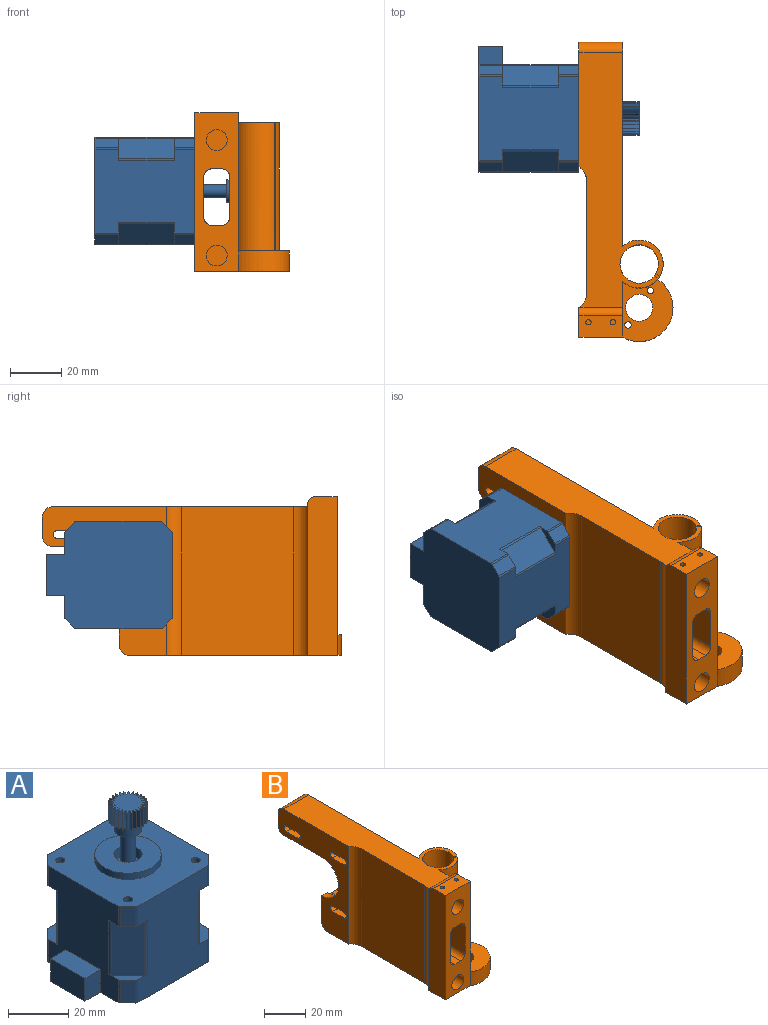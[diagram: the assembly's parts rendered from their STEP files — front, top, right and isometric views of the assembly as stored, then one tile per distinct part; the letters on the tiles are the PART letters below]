
ASSEMBLY  parts=2 mates=1
PART A: 123 faces, bbox 49.2x42x62.5 mm
  f0: cylinder r=2.5mm len=14mm, axis (0,0,-1), area 219.9mm2, adj f66,f68
  f1: plane 42x42mm, normal (0,0,1), area 1319.4mm2, adj f5,f7,f9,f11,f22,f23,f24,f25
  f2: plane 8.9x8.9mm, normal (0,0,1), area 27mm2, adj f5,f11,f12,f15,f35,f42,f49,f50
  f3: plane 8.9x8.9mm, normal (0,0,1), area 27mm2, adj f7,f8,f9,f17,f38,f39,f45,f46
  f4: plane 8.9x8.9mm, normal (0,0,1), area 27mm2, adj f9,f10,f11,f18,f40,f41,f47,f48
  f5: plane 39x32.69mm, normal (0,1,0), area 1089.8mm2, adj f1,f2,f13,f14,f19,f20,f28,f33
  f6: plane 9.2x3.66mm, normal (-0.71,0.71,0), area 47.6mm2, adj f13,f14,f43,f44
  f7: plane 39x32.69mm, normal (-1,0,0), area 941.7mm2, adj f1,f3,f13,f14,f19,f26,f31,f34
  f8: plane 9.2x3.66mm, normal (-0.71,-0.71,0), area 47.6mm2, adj f3,f14,f45,f46
  f9: plane 39x32.69mm, normal (0,-1,0), area 1089.8mm2, adj f1,f3,f4,f14,f21,f26,f29,f32
  f10: plane 9.2x3.66mm, normal (0.71,-0.71,0), area 47.6mm2, adj f4,f14,f47,f48
  f11: plane 39x32.69mm, normal (1,0,0), area 1089.8mm2, adj f1,f2,f4,f14,f20,f21,f27,f30
  f12: plane 9.2x3.66mm, normal (0.71,0.71,0), area 47.6mm2, adj f2,f14,f49,f50
  f13: plane 8.9x8.9mm, normal (0,0,1), area 27mm2, adj f5,f6,f7,f16,f36,f37,f43,f44
  f14: plane 49.2x42mm, normal (0,0,-1), area 1843.7mm2, adj f5,f6,f7,f8,f9,f10,f11,f12
  f15: plane 21.8x7.9mm, normal (0.71,0.71,0), area 243.5mm2, adj f2,f20,f35,f42
  f16: plane 21.8x7.9mm, normal (-0.71,0.71,0), area 243.5mm2, adj f13,f19,f36,f37
  f17: plane 21.8x7.9mm, normal (-0.71,-0.71,0), area 243.5mm2, adj f3,f26,f38,f39
  f18: plane 21.8x7.9mm, normal (0.71,-0.71,0), area 243.5mm2, adj f4,f21,f40,f41
  f19: plane 8.9x8.9mm, normal (0,0,-1), area 27mm2, adj f5,f7,f16,f23,f33,f34,f36,f37
  f20: plane 8.9x8.9mm, normal (0,0,-1), area 27mm2, adj f5,f11,f15,f22,f27,f28,f35,f42
  f21: plane 8.9x8.9mm, normal (0,0,-1), area 27mm2, adj f9,f11,f18,f25,f29,f30,f40,f41
  f22: plane 8x3.66mm, normal (0.71,0.71,0), area 41.4mm2, adj f1,f20,f27,f28
  f23: plane 8x3.66mm, normal (-0.71,0.71,0), area 41.4mm2, adj f1,f19,f33,f34
  f24: plane 8x3.66mm, normal (-0.71,-0.71,0), area 41.4mm2, adj f1,f26,f31,f32
  f25: plane 8x3.66mm, normal (0.71,-0.71,0), area 41.4mm2, adj f1,f21,f29,f30
  f26: plane 8.9x8.9mm, normal (0,0,-1), area 27mm2, adj f7,f9,f17,f24,f31,f32,f38,f39
  f27: cylinder r=1mm len=8mm, axis (0,0,1), area 6.3mm2, adj f1,f11,f20,f22
  f28: cylinder r=1mm len=8mm, axis (0,0,-1), area 6.3mm2, adj f1,f5,f20,f22
  f29: cylinder r=1mm len=8mm, axis (0,0,-1), area 6.3mm2, adj f1,f9,f21,f25
  f30: cylinder r=1mm len=8mm, axis (0,0,-1), area 6.3mm2, adj f1,f11,f21,f25
  f31: cylinder r=1mm len=8mm, axis (0,0,-1), area 6.3mm2, adj f1,f7,f24,f26
  f32: cylinder r=1mm len=8mm, axis (0,0,1), area 6.3mm2, adj f1,f9,f24,f26
  f33: cylinder r=1mm len=8mm, axis (0,0,1), area 6.3mm2, adj f1,f5,f19,f23
  f34: cylinder r=1mm len=8mm, axis (0,0,1), area 6.3mm2, adj f1,f7,f19,f23
  f35: cylinder r=1mm len=21.8mm, axis (0,0,-1), area 17.1mm2, adj f2,f5,f15,f20
  f36: cylinder r=1mm len=21.8mm, axis (0,0,1), area 17.1mm2, adj f5,f13,f16,f19
  f37: cylinder r=1mm len=21.8mm, axis (0,0,1), area 17.1mm2, adj f7,f13,f16,f19
  f38: cylinder r=1mm len=21.8mm, axis (0,0,-1), area 17.1mm2, adj f3,f7,f17,f26
  f39: cylinder r=1mm len=21.8mm, axis (0,0,1), area 17.1mm2, adj f3,f9,f17,f26
  f40: cylinder r=1mm len=21.8mm, axis (0,0,-1), area 17.1mm2, adj f4,f9,f18,f21
  f41: cylinder r=1mm len=21.8mm, axis (0,0,-1), area 17.1mm2, adj f4,f11,f18,f21
  f42: cylinder r=1mm len=21.8mm, axis (0,0,1), area 17.1mm2, adj f2,f11,f15,f20
  f43: cylinder r=1mm len=9.2mm, axis (0,0,1), area 7.2mm2, adj f5,f6,f13,f14
  f44: cylinder r=1mm len=9.2mm, axis (0,0,1), area 7.2mm2, adj f6,f7,f13,f14
  f45: cylinder r=1mm len=9.2mm, axis (0,0,-1), area 7.2mm2, adj f3,f7,f8,f14
  f46: cylinder r=1mm len=9.2mm, axis (0,0,1), area 7.2mm2, adj f3,f8,f9,f14
  f47: cylinder r=1mm len=9.2mm, axis (0,0,-1), area 7.2mm2, adj f4,f9,f10,f14
  f48: cylinder r=1mm len=9.2mm, axis (0,0,-1), area 7.2mm2, adj f4,f10,f11,f14
  f49: cylinder r=1mm len=9.2mm, axis (0,0,1), area 7.2mm2, adj f2,f11,f12,f14
  f50: cylinder r=1mm len=9.2mm, axis (0,0,-1), area 7.2mm2, adj f2,f5,f12,f14
  f51: plane 16.1x7.2mm, normal (0,0,1), area 115.9mm2, adj f7,f52,f53,f54
  f52: plane 9.2x7.2mm, normal (0,1,0), area 66.2mm2, adj f7,f14,f51,f54
  f53: plane 9.2x7.2mm, normal (0,-1,0), area 66.2mm2, adj f7,f14,f51,f54
  f54: plane 16.1x9.2mm, normal (-1,0,0), area 148.1mm2, adj f14,f51,f52,f53
  f55: cylinder r=1.5mm len=5.6mm, axis (0,0,1), area 52.8mm2, adj f1,f56
  f56: plane 3x3mm, normal (0,0,1), area 7.1mm2, adj f55
  f57: cylinder r=1.5mm len=5.6mm, axis (0,0,1), area 52.8mm2, adj f1,f58
  f58: plane 3x3mm, normal (0,0,1), area 7.1mm2, adj f57
  f59: cylinder r=1.5mm len=5.6mm, axis (0,0,1), area 52.8mm2, adj f1,f60
  f60: plane 3x3mm, normal (0,0,1), area 7.1mm2, adj f59
  f61: cylinder r=1.5mm len=5.6mm, axis (0,0,1), area 52.8mm2, adj f1,f62
  f62: plane 3x3mm, normal (0,0,1), area 7.1mm2, adj f61
  f63: cylinder r=11mm len=22mm, axis (0,0,-1), area 172.8mm2, adj f1,f64
  f64: plane 22x22mm, normal (0,0,1), area 312.2mm2, adj f63,f65
  f65: cylinder r=4.65mm len=9.3mm, axis (0,0,1), area 116.9mm2, adj f64,f66
  f66: plane 9.3x9.3mm, normal (0,0,1), area 48.3mm2, adj f0,f65
  f67: cylinder r=4.5mm len=9mm, axis (0,0,1), area 113.1mm2, adj f68,f72
  f68: plane 9x9mm, normal (0,0,-1), area 44mm2, adj f0,f67
  f69: plane 12.99x12.95mm, normal (0,0,1), area 96.3mm2, adj f70,f71,f73,f74,f75,f76,f77,f78
  f70: plane 7x1.39mm, normal (-0.73,0.68,0), area 13.3mm2, adj f69,f71,f72,f122
  f71: plane 7x1.85mm, normal (0.21,-0.98,0), area 13.3mm2, adj f69,f70,f72,f73
  f72: plane 12.99x12.95mm, normal (0,0,-1), area 32.7mm2, adj f67,f70,f71,f73,f74,f75,f76,f77
  f73: plane 7x1.66mm, normal (-0.87,0.49,0), area 13.3mm2, adj f69,f71,f72,f74
  f74: plane 7x1.71mm, normal (0.44,-0.9,0), area 13.3mm2, adj f69,f72,f73,f75
  f75: plane 7x1.83mm, normal (-0.96,0.26,0), area 13.3mm2, adj f69,f72,f74,f76
  f76: plane 7x1.46mm, normal (0.64,-0.77,0), area 13.3mm2, adj f69,f72,f75,f77
  f77: plane 7x1.89mm, normal (-1,0.03,0), area 13.3mm2, adj f69,f72,f76,f78
  f78: plane 7x1.52mm, normal (0.8,-0.59,0), area 13.3mm2, adj f69,f72,f77,f79
  f79: plane 7x1.85mm, normal (-0.98,-0.21,0), area 13.3mm2, adj f69,f72,f78,f80
  f80: plane 7x1.75mm, normal (0.92,-0.38,0), area 13.3mm2, adj f69,f72,f79,f81
  f81: plane 7x1.7mm, normal (-0.9,-0.44,0), area 13.3mm2, adj f69,f72,f80,f82
  f82: plane 7x1.87mm, normal (0.99,-0.15,0), area 13.3mm2, adj f69,f72,f81,f83
  f83: plane 7x1.45mm, normal (-0.76,-0.64,0), area 13.3mm2, adj f69,f72,f82,f84
  f84: plane 7x1.89mm, normal (1,0.09,0), area 13.3mm2, adj f69,f72,f83,f85
  f85: plane 7x1.53mm, normal (-0.59,-0.81,0), area 13.3mm2, adj f69,f72,f84,f86
  f86: plane 7x1.79mm, normal (0.95,0.32,0), area 13.3mm2, adj f69,f72,f85,f87
  f87: plane 7x1.75mm, normal (-0.38,-0.93,0), area 13.3mm2, adj f69,f72,f86,f88
  f88: plane 7x1.59mm, normal (0.84,0.54,0), area 13.3mm2, adj f69,f72,f87,f89
  f89: plane 7x1.87mm, normal (-0.15,-0.99,0), area 13.3mm2, adj f69,f72,f88,f90
  f90: plane 7x1.38mm, normal (0.69,0.73,0), area 13.3mm2, adj f69,f72,f89,f91
  f91: plane 7x1.89mm, normal (0.1,-1,0), area 13.3mm2, adj f69,f72,f90,f92
  f92: plane 7x1.65mm, normal (0.49,0.87,0), area 13.3mm2, adj f69,f72,f91,f93
  f93: plane 7x1.79mm, normal (0.33,-0.94,0), area 13.3mm2, adj f69,f72,f92,f94
  f94: plane 7x1.82mm, normal (0.27,0.96,0), area 13.3mm2, adj f69,f72,f93,f95
  f95: plane 7x1.59mm, normal (0.55,-0.84,0), area 13.3mm2, adj f69,f72,f94,f96
  f96: plane 7x1.89mm, normal (0.03,1,0), area 13.3mm2, adj f69,f72,f95,f97
  f97: plane 7x1.39mm, normal (0.73,-0.68,0), area 13.3mm2, adj f69,f72,f96,f98
  f98: plane 7x1.85mm, normal (-0.21,0.98,0), area 13.3mm2, adj f69,f72,f97,f99
  f99: plane 7x1.66mm, normal (0.87,-0.49,0), area 13.3mm2, adj f69,f72,f98,f100
  f100: plane 7x1.71mm, normal (-0.44,0.9,0), area 13.3mm2, adj f69,f72,f99,f101
  f101: plane 7x1.83mm, normal (0.96,-0.26,0), area 13.3mm2, adj f69,f72,f100,f102
  f102: plane 7x1.46mm, normal (-0.64,0.77,0), area 13.3mm2, adj f69,f72,f101,f103
  f103: plane 7x1.89mm, normal (1,-0.03,0), area 13.3mm2, adj f69,f72,f102,f104
  f104: plane 7x1.52mm, normal (-0.8,0.59,0), area 13.3mm2, adj f69,f72,f103,f105
  f105: plane 7x1.85mm, normal (0.98,0.21,0), area 13.3mm2, adj f69,f72,f104,f106
  f106: plane 7x1.75mm, normal (-0.92,0.38,0), area 13.3mm2, adj f69,f72,f105,f107
  f107: plane 7x1.7mm, normal (0.9,0.44,0), area 13.3mm2, adj f69,f72,f106,f108
  f108: plane 7x1.87mm, normal (-0.99,0.15,0), area 13.3mm2, adj f69,f72,f107,f109
  f109: plane 7x1.45mm, normal (0.76,0.64,0), area 13.3mm2, adj f69,f72,f108,f110
  f110: plane 7x1.89mm, normal (-1,-0.09,0), area 13.3mm2, adj f69,f72,f109,f111
  f111: plane 7x1.53mm, normal (0.59,0.81,0), area 13.3mm2, adj f69,f72,f110,f112
  f112: plane 7x1.79mm, normal (-0.95,-0.32,0), area 13.3mm2, adj f69,f72,f111,f113
  f113: plane 7x1.75mm, normal (0.38,0.93,0), area 13.3mm2, adj f69,f72,f112,f114
  f114: plane 7x1.59mm, normal (-0.84,-0.54,0), area 13.3mm2, adj f69,f72,f113,f115
  f115: plane 7x1.87mm, normal (0.15,0.99,0), area 13.3mm2, adj f69,f72,f114,f116
  f116: plane 7x1.38mm, normal (-0.69,-0.73,0), area 13.3mm2, adj f69,f72,f115,f117
  f117: plane 7x1.89mm, normal (-0.1,1,0), area 13.3mm2, adj f69,f72,f116,f118
  f118: plane 7x1.65mm, normal (-0.49,-0.87,0), area 13.3mm2, adj f69,f72,f117,f119
  f119: plane 7x1.79mm, normal (-0.33,0.94,0), area 13.3mm2, adj f69,f72,f118,f120
  f120: plane 7x1.82mm, normal (-0.27,-0.96,0), area 13.3mm2, adj f69,f72,f119,f121
  f121: plane 7x1.59mm, normal (-0.55,0.84,0), area 13.3mm2, adj f69,f72,f120,f122
  f122: plane 7x1.89mm, normal (-0.03,-1,0), area 13.3mm2, adj f69,f70,f72,f121
PART B: 73 faces, bbox 36.7x116.7x62 mm
  f0: plane 99.5x32.86mm, normal (0,0,1), area 1607.2mm2, adj f1,f16,f17,f18,f19,f20,f21,f22
  f1: plane 79.76x58mm, normal (1,0,0), area 2945.1mm2, adj f0,f15,f20,f24,f33,f34,f35,f44
  f2: cylinder r=1.6mm len=15mm, axis (-1,0,0), area 75.4mm2, adj f3,f5,f21,f61
  f3: plane 15x7.89mm, normal (0,0,-1), area 118.4mm2, adj f2,f4,f21,f61
  f4: cylinder r=1.6mm len=15mm, axis (-1,0,0), area 75.4mm2, adj f3,f5,f21,f61
  f5: plane 15x7.89mm, normal (0,0,1), area 118.4mm2, adj f2,f4,f21,f61
  f6: cylinder r=1.6mm len=15mm, axis (-1,0,0), area 75.4mm2, adj f7,f9,f21,f56
  f7: plane 15x8mm, normal (0,0,-1), area 120mm2, adj f6,f8,f21,f56
  f8: cylinder r=1.6mm len=15mm, axis (-1,0,0), area 75.4mm2, adj f7,f9,f21,f56
  f9: plane 15x8mm, normal (0,0,1), area 120mm2, adj f6,f8,f21,f56
  f10: cylinder r=1.6mm len=15mm, axis (-1,0,0), area 75.4mm2, adj f11,f13,f21,f51
  f11: plane 15x8mm, normal (0,0,-1), area 120mm2, adj f10,f12,f21,f51
  f12: cylinder r=1.6mm len=15mm, axis (-1,0,0), area 75.4mm2, adj f11,f13,f21,f51
  f13: plane 15x8mm, normal (0,0,1), area 120mm2, adj f10,f12,f21,f51
  f14: plane 62x17mm, normal (0,-1,0), area 737.3mm2, adj f16,f23,f24,f25,f36,f37,f38,f39
  f15: plane 17x15.5mm, normal (0,1,0), area 252mm2, adj f1,f21,f35,f36,f46,f69,f72
  f16: plane 54x21.76mm, normal (1,0,0), area 1132mm2, adj f0,f14,f20,f29,f62,f65,f68
  f17: plane 57x1.46mm, normal (0.63,0.78,0), area 106.6mm2, adj f0,f18,f20,f30
  f18: cylinder r=7.49mm len=58mm, axis (0,0,-1), area 2677.8mm2, adj f0,f17,f19,f24,f30
  f19: plane 57x1.47mm, normal (-0.63,-0.78,0), area 107.5mm2, adj f0,f18,f20,f30
  f20: cylinder r=9.36mm len=58mm, axis (0,0,-1), area 2363.1mm2, adj f0,f1,f16,f17,f19,f24,f25,f29
  f21: plane 58x48.5mm, normal (-1,0,0), area 1219.4mm2, adj f0,f2,f3,f4,f5,f6,f7,f8
  f22: plane 58x43.76mm, normal (-1,0,0), area 2538.3mm2, adj f0,f24,f31,f32
  f23: plane 62x11.5mm, normal (-1,0,0), area 711.1mm2, adj f14,f24,f32,f62,f65,f68
  f24: plane 82.71x36.71mm, normal (0,0,-1), area 1581.7mm2, adj f1,f14,f18,f20,f21,f22,f23,f25
  f25: cylinder r=13.21mm len=24.26mm, axis (0,0,-1), area 325.1mm2, adj f14,f20,f24,f29
  f26: cylinder r=1.22mm len=8mm, axis (0,0,-1), area 61.6mm2, adj f24,f29
  f27: cylinder r=1.25mm len=8mm, axis (0,0,-1), area 62.8mm2, adj f24,f29
  f28: cylinder r=5.25mm len=10.5mm, axis (0,0,-1), area 263.9mm2, adj f24,f29
  f29: plane 24.26x19.71mm, normal (0,0,1), area 287.3mm2, adj f16,f20,f25,f26,f27,f28
  f30: plane 1.99x1.94mm, normal (0,0,1), area 1.7mm2, adj f17,f18,f19,f20
  f31: cylinder r=6.76mm len=58mm, axis (0,0,1), area 384.6mm2, adj f0,f21,f22,f24
  f32: cylinder r=6.76mm len=58mm, axis (0,0,1), area 384.6mm2, adj f0,f22,f23,f24
  f33: plane 26x17mm, normal (0,0,-1), area 442mm2, adj f1,f21,f35,f45
  f34: plane 17x7.5mm, normal (0,1,0), area 127.5mm2, adj f1,f21,f44,f45
  f35: cylinder r=11.5mm len=23mm, axis (-1,0,0), area 338.2mm2, adj f1,f15,f21,f33,f37,f38,f39,f69
  f36: plane 85x4mm, normal (0,0,1), area 340mm2, adj f14,f15,f69,f72
  f37: plane 79.32x16mm, normal (-1,0,0), area 1196.2mm2, adj f14,f35,f69,f70
  f38: plane 77.84x4mm, normal (0,0,-1), area 311.4mm2, adj f14,f35,f70,f71
  f39: plane 79.32x16mm, normal (1,0,0), area 1196.2mm2, adj f14,f35,f71,f72
  f40: cylinder r=4.08mm len=10mm, axis (0,-1,0), area 256.1mm2, adj f14,f41
  f41: plane 8.15x8.15mm, normal (0,-1,0), area 52.2mm2, adj f40
  f42: cylinder r=4.08mm len=10mm, axis (0,-1,0), area 256.1mm2, adj f14,f43
  f43: plane 8.15x8.15mm, normal (0,-1,0), area 52.2mm2, adj f42
  f44: cylinder r=4mm len=17mm, axis (-1,0,0), area 106.8mm2, adj f0,f1,f21,f34
  f45: cylinder r=4mm len=17mm, axis (1,0,0), area 106.8mm2, adj f1,f21,f33,f34
  f46: cylinder r=4mm len=17mm, axis (-1,0,0), area 106.8mm2, adj f1,f15,f21,f24
  f47: plane 8x2mm, normal (0,0,1), area 16mm2, adj f1,f48,f50,f51
  f48: cylinder r=2.6mm len=5.2mm, axis (1,0,0), area 16.3mm2, adj f1,f47,f49,f51
  f49: plane 8x2mm, normal (0,0,-1), area 16mm2, adj f1,f48,f50,f51
  f50: cylinder r=2.6mm len=5.2mm, axis (1,0,0), area 16.3mm2, adj f1,f47,f49,f51
  f51: plane 13.2x5.2mm, normal (1,0,0), area 29.2mm2, adj f10,f11,f12,f13,f47,f48,f49,f50
  f52: plane 8x2mm, normal (0,0,1), area 16mm2, adj f1,f53,f55,f56
  f53: cylinder r=2.6mm len=5.2mm, axis (1,0,0), area 16.3mm2, adj f1,f52,f54,f56
  f54: plane 8x2mm, normal (0,0,-1), area 16mm2, adj f1,f53,f55,f56
  f55: cylinder r=2.6mm len=5.2mm, axis (1,0,0), area 16.3mm2, adj f1,f52,f54,f56
  f56: plane 13.2x5.2mm, normal (1,0,0), area 29.2mm2, adj f6,f7,f8,f9,f52,f53,f54,f55
  f57: plane 7.89x2mm, normal (0,0,1), area 15.8mm2, adj f1,f58,f60,f61
  f58: cylinder r=2.6mm len=5.2mm, axis (1,0,0), area 16.3mm2, adj f1,f57,f59,f61
  f59: plane 7.89x2mm, normal (0,0,-1), area 15.8mm2, adj f1,f58,f60,f61
  f60: cylinder r=2.6mm len=5.2mm, axis (1,0,0), area 16.3mm2, adj f1,f57,f59,f61
  f61: plane 13.09x5.2mm, normal (1,0,0), area 29mm2, adj f2,f3,f4,f5,f57,f58,f59,f60
  f62: plane 17x1mm, normal (0,1,0), area 17mm2, adj f0,f16,f23,f68
  f63: cylinder r=1.05mm len=4mm, axis (0,0,-1), area 26.4mm2, adj f65,f67
  f64: cylinder r=1.05mm len=4mm, axis (0,0,-1), area 26.4mm2, adj f65,f66
  f65: plane 17x8.5mm, normal (0,0,1), area 137.6mm2, adj f14,f16,f23,f63,f64,f68
  f66: plane 2.1x2.1mm, normal (0,0,1), area 3.5mm2, adj f64
  f67: plane 2.1x2.1mm, normal (0,0,1), area 3.5mm2, adj f63
  f68: cylinder r=3mm len=17mm, axis (1,0,0), area 80.1mm2, adj f16,f23,f62,f65
  f69: cylinder r=3mm len=85mm, axis (0,-1,0), area 394.6mm2, adj f14,f15,f35,f36,f37
  f70: cylinder r=3mm len=77.84mm, axis (0,1,0), area 361.7mm2, adj f14,f35,f37,f38
  f71: cylinder r=3mm len=77.84mm, axis (0,-1,0), area 361.7mm2, adj f14,f35,f38,f39
  f72: cylinder r=3mm len=85mm, axis (0,1,0), area 394.6mm2, adj f14,f15,f35,f36,f39
PLACE A rot(axis=(-0.58,0.58,-0.58),120deg) t=(-67.98,95.38,17.82)mm
PLACE B t=(32.89,-0.93,27.61)mm
MATE fastened A.f57 <-> B.f2  axis (1,0,0) through (-28.98,28.79,12.11)mm
